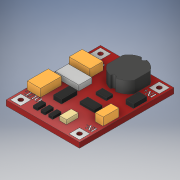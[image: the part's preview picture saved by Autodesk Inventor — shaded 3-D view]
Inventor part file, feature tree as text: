
AUTODESK INVENTOR PART (.ipt)
format: ipt  version: 2019.4 (Build 234330000, 330)  size: 941,568 bytes
history: native  units: mm
features: extrude x7, sketch x2, emboss x1, other x1
ambient origin geometry x8: Origin, YZ Plane, XZ Plane, XY Plane, X Axis, Y Axis, Z Axis, Center Point
bodies: Solid1 (feature_tree)
feature tree (11):
  sketch  "Sketch1"  dims[d0=14.0mm d1=18.0mm]
  extrude  "Extrusion1"  Depth=18.0mm
  extrude  "Extrusion2"  Depth=0.01mm
  extrude  "Extrusion3"  Depth=0.01mm
  extrude  "Extrusion4"  Depth=0.01mm
  extrude  "Extrusion5"  Depth=0.01mm
  extrude  "Extrusion6"  Depth=0.01mm
  extrude  "Extrusion7"  Depth=0.01mm
  emboss  "Emboss1"
  other  "Image1"
  sketch  "Sketch2"  dims[d26=2.0mm d33=0.4mm d34=0.4mm d35=0.4mm d36=0.4mm d37=0.4mm d38=0.4mm d39=0.4mm d44=0.4mm d45=0.85mm d47=1.0mm d50=1.0mm d51=1.0mm d52=1.0mm d59=2.5mm d60=4.0mm d62=0.4mm d63=1.25mm d64=4.0mm d65=2.5mm d67=0.4mm d68=1.5mm d69=6.0mm d71=0.5mm d72=0.5mm d74=3.0mm d76=3.25mm d77=3.0mm d78=3.0mm d80=3.0mm d83=1.5mm d84=3.0mm d85=0.4mm d86=2.5mm d87=4.5mm d88=2.5mm d89=1.0mm d90=2.0mm d91=1.25mm d95=2.25mm d96=1.0mm d97=2.75mm d98=1.5mm d100=1.6mm d101=2.3mm d102=1.5mm d103=2.5mm d104=0.4mm d105=2.8mm d106=1.35mm d107=2.25mm d110=2.35mm d111=1.75mm d112=1.6mm d113=0.8mm d114=0.8mm d115=1.2mm d117=0.65mm d118=0.65mm d119=1.5mm d120=3.0mm d122=0.8mm d123=1.6mm d124=1.0mm d125=0.0mm d126=0.01mm d127=0.0mm d128=1.5mm d129=0.0mm d130=1.0mm d131=0.0mm d132=0.8mm d133=0.0mm d134=0.5mm d135=0.0mm d136=2.25mm d137=0.0mm d138=0.5mm d139=0.5mm d140=0.2mm d141=0.01mm d142=0.0mm]
